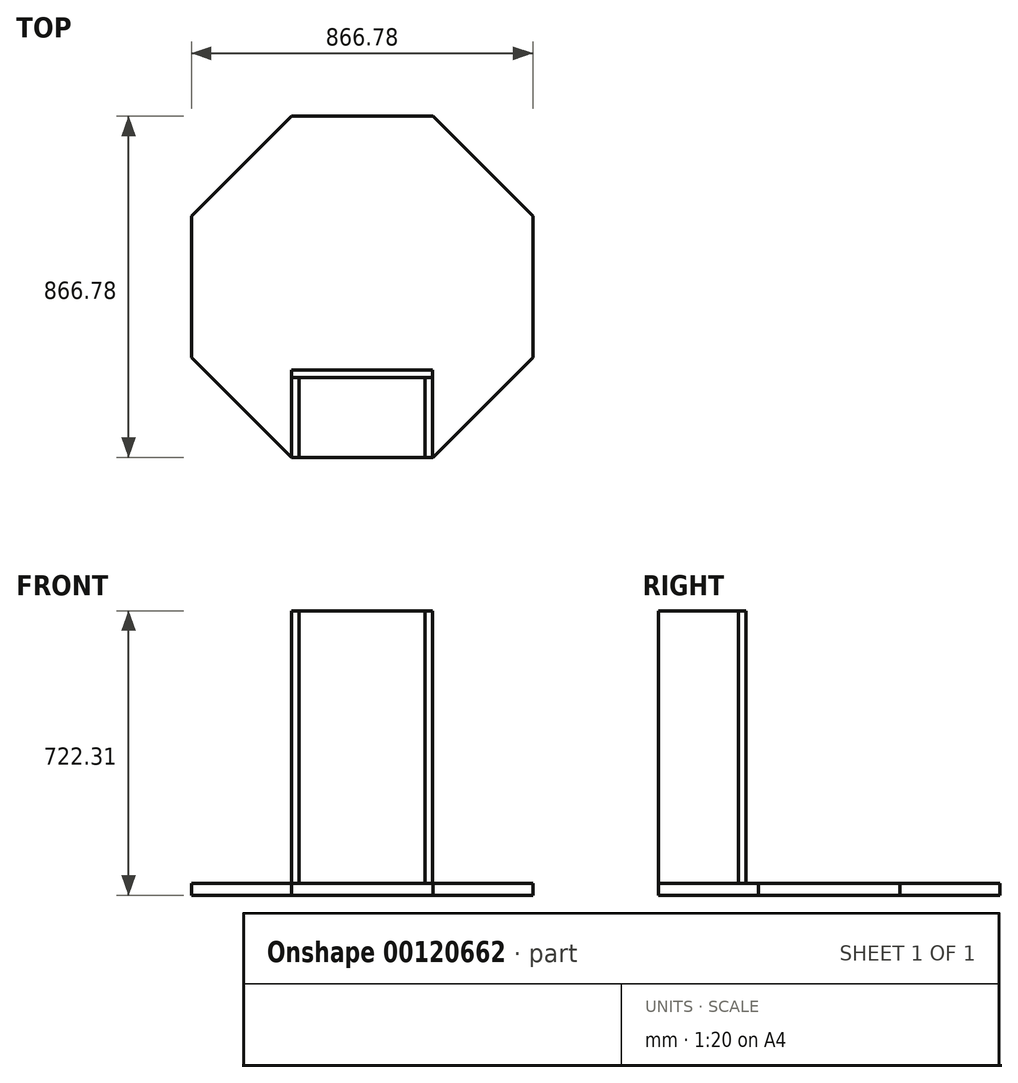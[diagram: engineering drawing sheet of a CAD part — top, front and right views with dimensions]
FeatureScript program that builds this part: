
annotation { "Feature Type Name" : "Feature", "Feature Type Description" : "" }
export const myFeature = defineFeature(function(context is Context, id is Id, definition is map)
    precondition{}
    {
        {
            var Q0;
            Q0=qCreatedBy(makeId("Top.planeOp"),FACE);
            var sketch = newSketch(context, id + "F0", { "sketchPlane" : qUnion([Q0])});
            skCircle(sketch, "E0.cCircle", {"center": v(0, 0) * mm, "radius": 469.1 * mm, "construction": true});
            skLineSegment(sketch, "E0.0", {"start": v(179.51, -433.39) * mm, "end": v(-179.51, -433.39) * mm});
            skLineSegment(sketch, "E0.1", {"start": v(-179.51, -433.39) * mm, "end": v(-433.39, -179.51) * mm});
            skLineSegment(sketch, "E0.2", {"start": v(-433.39, -179.51) * mm, "end": v(-433.39, 179.51) * mm});
            skLineSegment(sketch, "E0.3", {"start": v(-433.39, 179.51) * mm, "end": v(-179.51, 433.39) * mm});
            skLineSegment(sketch, "E0.4", {"start": v(-179.51, 433.39) * mm, "end": v(179.51, 433.39) * mm});
            skLineSegment(sketch, "E0.5", {"start": v(179.51, 433.39) * mm, "end": v(433.39, 179.51) * mm});
            skLineSegment(sketch, "E0.6", {"start": v(433.39, 179.51) * mm, "end": v(433.39, -179.51) * mm});
            skLineSegment(sketch, "E0.7", {"start": v(433.39, -179.51) * mm, "end": v(179.51, -433.39) * mm});
            skSolve(sketch);
        }
        {
            var Q0;
            Q0=makeQuery(id+"F0.imprint","IMPRINT",FACE,{"disambiguationData":[TD([[makeQuery(id+"F0.imprint","IMPRINT",EDGE,{"derivedFrom":sQuery(id+"F0.wireOp",EDGE,"E0.0")}),-1.0]])]});
            extrude(context, id + "F1", {"entities" : qUnion([Q0]), "depth" : 30.16 * mm});
        }
        {
            var Q0;
            Q0=makeQuery(id+"F1.opExtrude","CAP_FACE",FACE,{"disambiguationData":[OSD([sQuery(id+"F0.wireOp",EDGE,"E0.0"),sQuery(id+"F0.wireOp",EDGE,"E0.1"),sQuery(id+"F0.wireOp",EDGE,"E0.2"),sQuery(id+"F0.wireOp",EDGE,"E0.3"),sQuery(id+"F0.wireOp",EDGE,"E0.4"),sQuery(id+"F0.wireOp",EDGE,"E0.5"),sQuery(id+"F0.wireOp",EDGE,"E0.6"),sQuery(id+"F0.wireOp",EDGE,"E0.7")])],"isStart":false});
            var sketch = newSketch(context, id + "F2", { "sketchPlane" : qUnion([Q0])});
            skLineSegment(sketch, "E1.bottom", {"start": v(-179.51, -433.39) * mm, "end": v(-160.46, -433.39) * mm});
            skLineSegment(sketch, "E1.top", {"start": v(-179.51, -230.19) * mm, "end": v(-160.46, -230.19) * mm});
            skLineSegment(sketch, "E1.left", {"start": v(-179.51, -433.39) * mm, "end": v(-179.51, -230.19) * mm});
            skLineSegment(sketch, "E1.right", {"start": v(-160.46, -433.39) * mm, "end": v(-160.46, -230.19) * mm});
            skSolve(sketch);
        }
        {
            var Q0;
            Q0=makeQuery(id+"F2.imprint","IMPRINT",FACE,{"disambiguationData":[TD([[makeQuery(id+"F2.imprint","IMPRINT",EDGE,{"derivedFrom":sQuery(id+"F2.wireOp",EDGE,"E1.bottom")}),-1.0]])]});
            extrude(context, id + "F3", {"entities" : qUnion([Q0]), "depth" : 692.15 * mm});
        }
        {
            var Q0;
            Q0=makeQuery(id+"F1.opExtrude","CAP_FACE",FACE,{"disambiguationData":[OSD([sQuery(id+"F0.wireOp",EDGE,"E0.0"),sQuery(id+"F0.wireOp",EDGE,"E0.1"),sQuery(id+"F0.wireOp",EDGE,"E0.2"),sQuery(id+"F0.wireOp",EDGE,"E0.3"),sQuery(id+"F0.wireOp",EDGE,"E0.4"),sQuery(id+"F0.wireOp",EDGE,"E0.5"),sQuery(id+"F0.wireOp",EDGE,"E0.6"),sQuery(id+"F0.wireOp",EDGE,"E0.7")])],"isStart":false});
            var sketch = newSketch(context, id + "F4", { "sketchPlane" : qUnion([Q0])});
            skLineSegment(sketch, "E2.bottom", {"start": v(-179.51, -230.19) * mm, "end": v(179.26, -230.19) * mm});
            skLineSegment(sketch, "E2.top", {"start": v(-179.51, -211.14) * mm, "end": v(179.26, -211.14) * mm});
            skLineSegment(sketch, "E2.left", {"start": v(-179.51, -230.19) * mm, "end": v(-179.51, -211.14) * mm});
            skLineSegment(sketch, "E2.right", {"start": v(179.26, -230.19) * mm, "end": v(179.26, -211.14) * mm});
            skSolve(sketch);
        }
        {
            var Q0;
            Q0=makeQuery(id+"F4.imprint","IMPRINT",FACE,{"disambiguationData":[TD([[makeQuery(id+"F4.imprint","IMPRINT",EDGE,{"derivedFrom":sQuery(id+"F4.wireOp",EDGE,"E2.bottom")}),1.0]])]});
            extrude(context, id + "F5", {"entities" : qUnion([Q0]), "depth" : 692.15 * mm});
        }
        {
            var Q0;
            Q0=makeQuery(id+"F3.opExtrude","SWEPT_BODY",BODY,{"disambiguationData":[OSD([sQuery(id+"F2.wireOp",EDGE,"E1.bottom"),sQuery(id+"F2.wireOp",EDGE,"E1.top"),sQuery(id+"F2.wireOp",EDGE,"E1.left"),sQuery(id+"F2.wireOp",EDGE,"E1.right")])]});
            transform(context, id + "F6", {"entities" : qUnion([Q0]), "transformType" : TransformType.TRANSLATION_3D, "dx" : 339.72 * mm, "dy" : 0 * mm, "dz" : 0 * mm, "makeCopy" : true});
        }
    });
